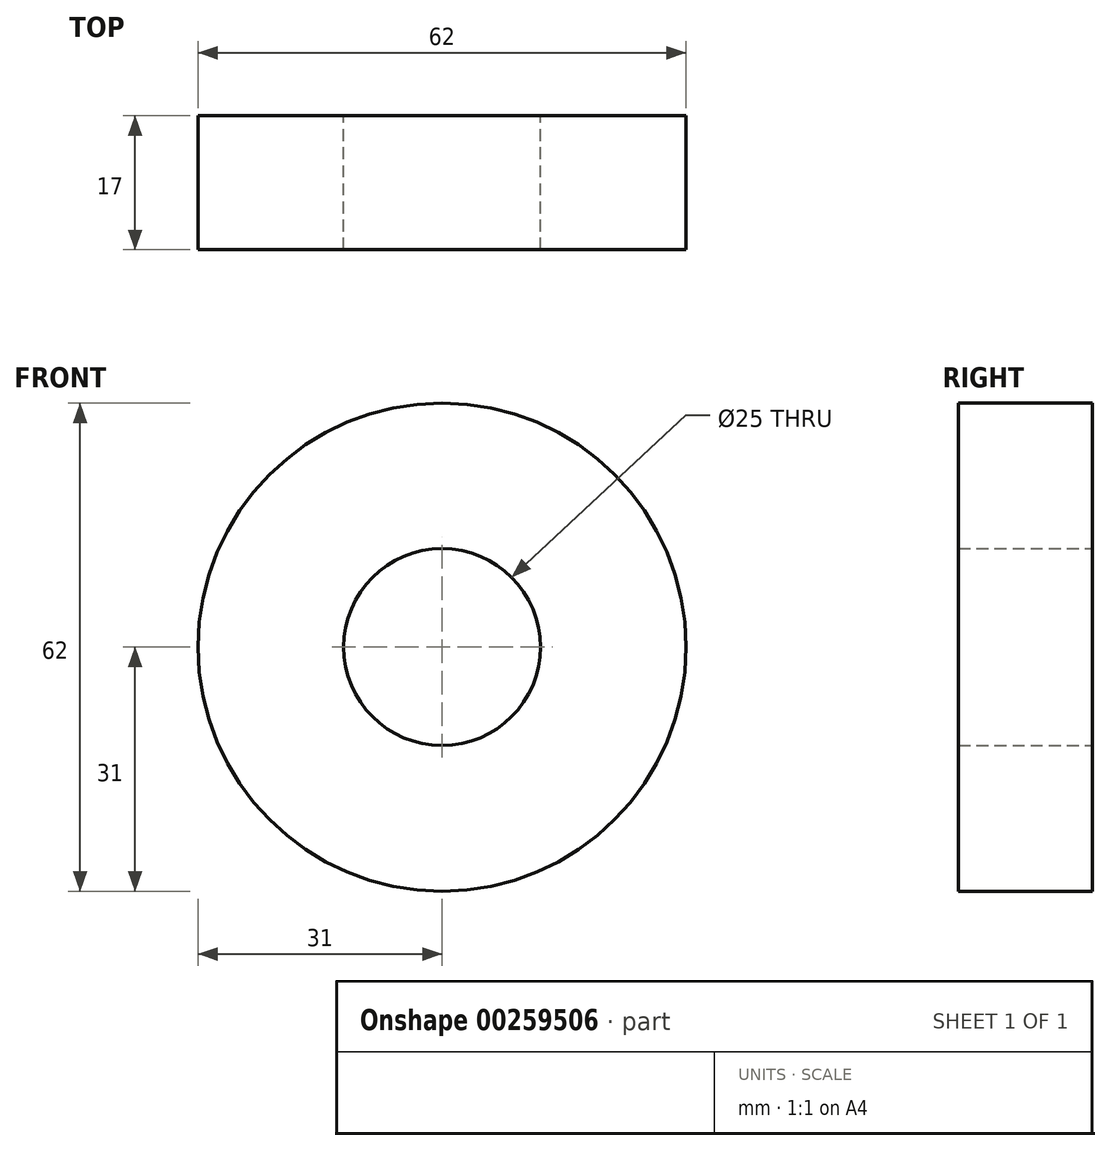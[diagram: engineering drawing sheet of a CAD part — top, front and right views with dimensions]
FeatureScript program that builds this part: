
annotation { "Feature Type Name" : "Feature", "Feature Type Description" : "" }
export const myFeature = defineFeature(function(context is Context, id is Id, definition is map)
    precondition{}
    {
        {
            var Q0;
            Q0=qCreatedBy(makeId("Front.planeOp"),FACE);
            var sketch = newSketch(context, id + "F0", { "sketchPlane" : qUnion([Q0])});
            skCircle(sketch, "E0", {"center": v(0, 0) * mm, "radius": 12.5 * mm});
            skCircle(sketch, "E1", {"center": v(0, 0) * mm, "radius": 31 * mm});
            skSolve(sketch);
        }
        {
            var Q0;
            Q0 = qSketchRegion(id + "F0", true);
            extrude(context, id + "F1", {"entities" : qUnion([Q0]), "depth" : 17 * mm});
        }
    });
